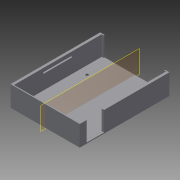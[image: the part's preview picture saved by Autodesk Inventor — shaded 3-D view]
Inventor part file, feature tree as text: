
AUTODESK INVENTOR PART (.ipt)
format: ipt  version: 2015 SP2 (Build 190223200, 223)  size: 185,856 bytes
history: native  units: in
note: dims shown in document units (in); Inventor stores cm internally (conversion verified against a paired STEP export)
features: sketch x9, extrude x7, projected_geometry x3, hole x1, plane x1, mirror x1
ambient origin geometry x8: Origin, YZ Plane, XZ Plane, XY Plane, X Axis, Y Axis, Z Axis, Center Point
bodies: Solid1 (feature_tree)
feature tree (22):
  extrude  "Extrusion1"  Depth=3.3465in
  sketch  "Sketch2"  dims[d2=0.1969in d3=0.0394in d4=0.0in]
  hole  "Hole1"  [1 undecoded]
  extrude  "Extrusion4"  Depth=3.3465in
  extrude  "Extrusion5"  Depth=0.1083in
  extrude  "Extrusion6"  Depth=0.1083in
  extrude  "Extrusion7"  Depth=2.2835in
  sketch  "Sketch8"  dims[d22=2.2835in d23=1.9291in]
  extrude  "Extrusion8"  Depth=1.9291in
  plane  "Work Plane2"
  mirror  "Mirror1"
  extrude  "Extrusion9"  Depth=0.2441in
  sketch  "Sketch1"  dims[d0=2.2047in d1=3.3465in]
  projected_geometry  "Projected Loop1"
  sketch  "Sketch4"  dims[d14=2.2047in d15=3.3465in]
  sketch  "Sketch5"  dims[d16=0.1083in d17=0.1083in]
  sketch  "Sketch6"  dims[d18=0.1083in d19=0.1083in]
  projected_geometry  "Projected Loop2"
  sketch  "Sketch7"  dims[d20=1.9291in d21=2.2835in]
  projected_geometry  "Projected Loop3"
  sketch  "Sketch9"  dims[d24=0.2441in d25=0.2441in]
  sketch  "Sketch10"  dims[d26=0.2441in d27=0.2441in d28=0.1378in d29=0.1378in d30=0.1378in d31=0.1378in d32=0.1378in d33=0.1083in d34=0.2362in d35=0.1575in d36=0.0787in d37=90.0deg d38=0.315in d39=0.8108in d41=0.0394in d42=0.7874in d43=0.0394in d44=0.0in d45=0.0in d46=0.0787in d47=0.0787in d48=0.0787in d49=0.0in d50=3.5433in d51=0.0591in d52=0.0in d53=0.0591in d54=0.0in d55=3.622in d56=2.7953in d59=0.0591in d60=0.0in d61=-1.3976in d62=0.1476in d63=0.0591in d64=1.1811in d65=1.1811in d66=1.1811in d67=0.2756in d68=0.7087in d69=0.6299in d70=0.1181in d71=0.0in d72=0.9843in]
note: 1 required parameter value undecoded (feature->parameter linkage not recoverable at this tier; creation-order binding heuristic only, values carry confidence <= 0.55)
